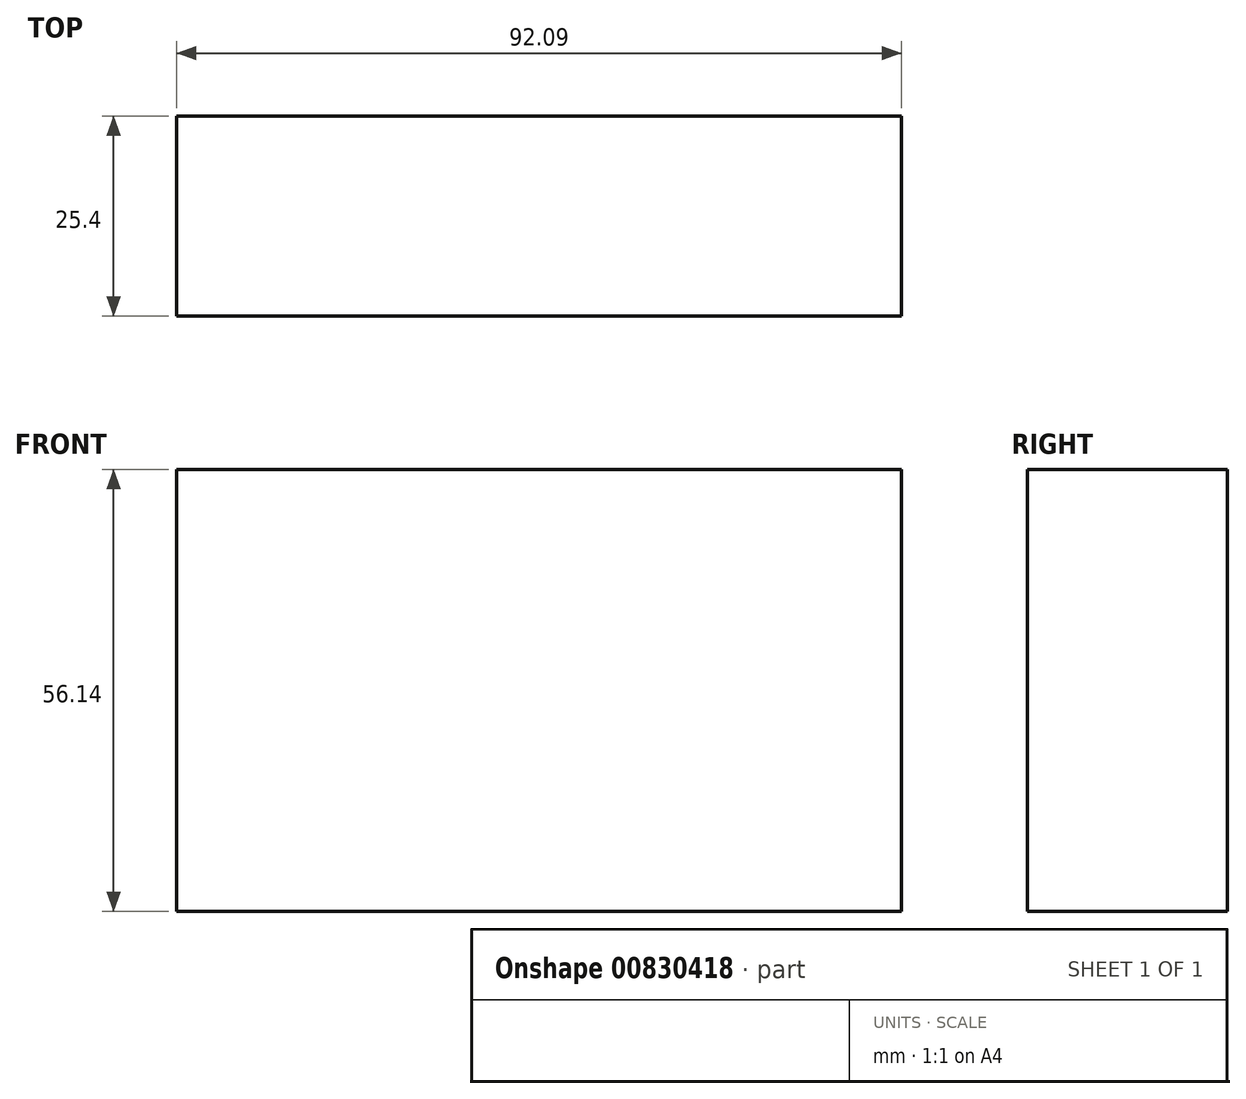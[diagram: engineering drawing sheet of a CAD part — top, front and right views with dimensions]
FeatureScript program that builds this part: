
annotation { "Feature Type Name" : "Feature", "Feature Type Description" : "" }
export const myFeature = defineFeature(function(context is Context, id is Id, definition is map)
    precondition{}
    {
        {
            var Q0;
            Q0=qCreatedBy(makeId("Front.planeOp"),FACE);
            var sketch = newSketch(context, id + "F0", { "sketchPlane" : qUnion([Q0])});
            skLineSegment(sketch, "E0.bottom", {"start": v(0, 0) * mm, "end": v(92.09, 0) * mm});
            skLineSegment(sketch, "E0.top", {"start": v(0, 56.14) * mm, "end": v(92.09, 56.14) * mm});
            skLineSegment(sketch, "E0.left", {"start": v(0, 0) * mm, "end": v(0, 56.14) * mm});
            skLineSegment(sketch, "E0.right", {"start": v(92.09, 0) * mm, "end": v(92.09, 56.14) * mm});
            skSolve(sketch);
        }
        {
            var Q0;
            Q0 = qSketchRegion(id + "F0", true);
            extrude(context, id + "F1", {"entities" : qUnion([Q0]), "depth" : 25.4 * mm, "offsetDistance" : 25.4 * mm});
        }
    });
